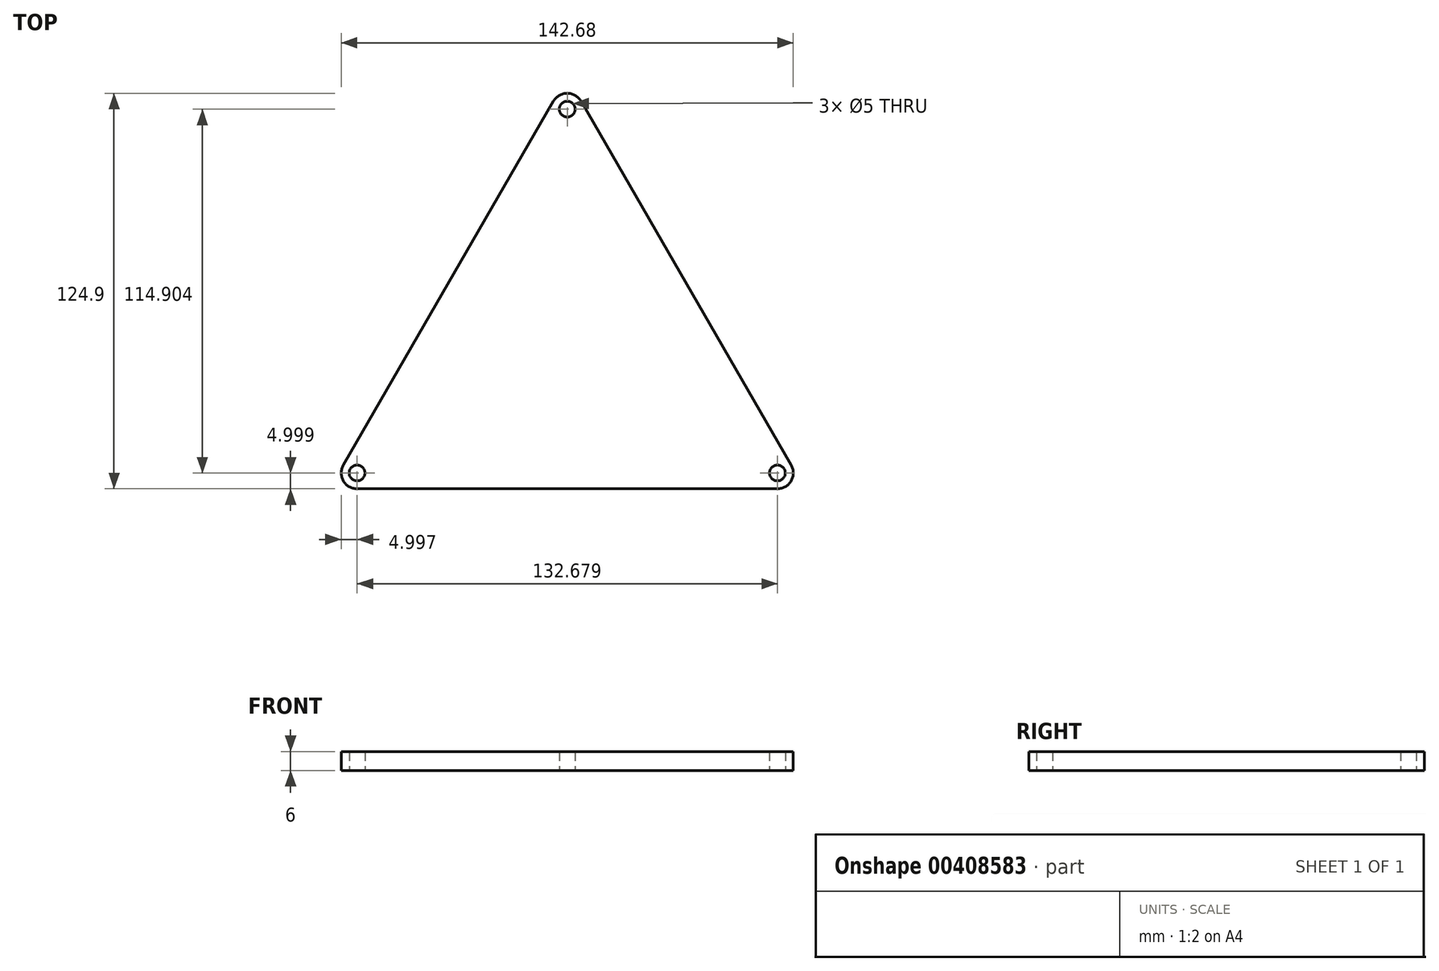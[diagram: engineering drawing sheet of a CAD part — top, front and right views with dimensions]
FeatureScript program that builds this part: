
annotation { "Feature Type Name" : "Feature", "Feature Type Description" : "" }
export const myFeature = defineFeature(function(context is Context, id is Id, definition is map)
    precondition{}
    {
        {
            var Q0;
            Q0=qCreatedBy(makeId("Top.planeOp"),FACE);
            var sketch = newSketch(context, id + "F0", { "sketchPlane" : qUnion([Q0])});
            skLineSegment(sketch, "E0", {"start": v(-3.86, 79.38) * mm, "end": v(-70.2, -35.52) * mm});
            skLineSegment(sketch, "E1", {"start": v(-65.87, -43.02) * mm, "end": v(66.8, -43.02) * mm});
            skLineSegment(sketch, "E2", {"start": v(71.14, -35.52) * mm, "end": v(4.8, 79.38) * mm});
            skPoint(sketch, "E3.visualSharp", {"position": v(0.47, 86.88) * mm});
            skArc(sketch, "E3.filletArc", {"start": v(4.8, 79.38) * mm, "mid": v(0.47, 81.88) * mm, "end": v(-3.86, 79.38) * mm});
            skPoint(sketch, "E4.visualSharp", {"position": v(-74.53, -43.02) * mm});
            skArc(sketch, "E4.filletArc", {"start": v(-70.2, -35.52) * mm, "mid": v(-70.2, -40.52) * mm, "end": v(-65.87, -43.02) * mm});
            skPoint(sketch, "E5.visualSharp", {"position": v(75.47, -43.02) * mm});
            skArc(sketch, "E5.filletArc", {"start": v(66.8, -43.02) * mm, "mid": v(71.14, -40.52) * mm, "end": v(71.14, -35.52) * mm});
            skCircle(sketch, "E6", {"center": v(0.47, 76.88) * mm, "radius": 2.5 * mm});
            skCircle(sketch, "E7", {"center": v(-65.87, -38.02) * mm, "radius": 2.5 * mm});
            skCircle(sketch, "E8", {"center": v(66.8, -38.02) * mm, "radius": 2.5 * mm});
            skSolve(sketch);
        }
        {
            var Q0;
            Q0=makeQuery(id+"F0.imprint","IMPRINT",FACE,{"disambiguationData":[TD([[makeQuery(id+"F0.imprint","IMPRINT",EDGE,{"derivedFrom":sQuery(id+"F0.wireOp",EDGE,"E0")}),1.0]])]});
            extrude(context, id + "F1", {"entities" : qUnion([Q0]), "depth" : 6 * mm, "offsetDistance" : 25 * mm});
        }
    });
